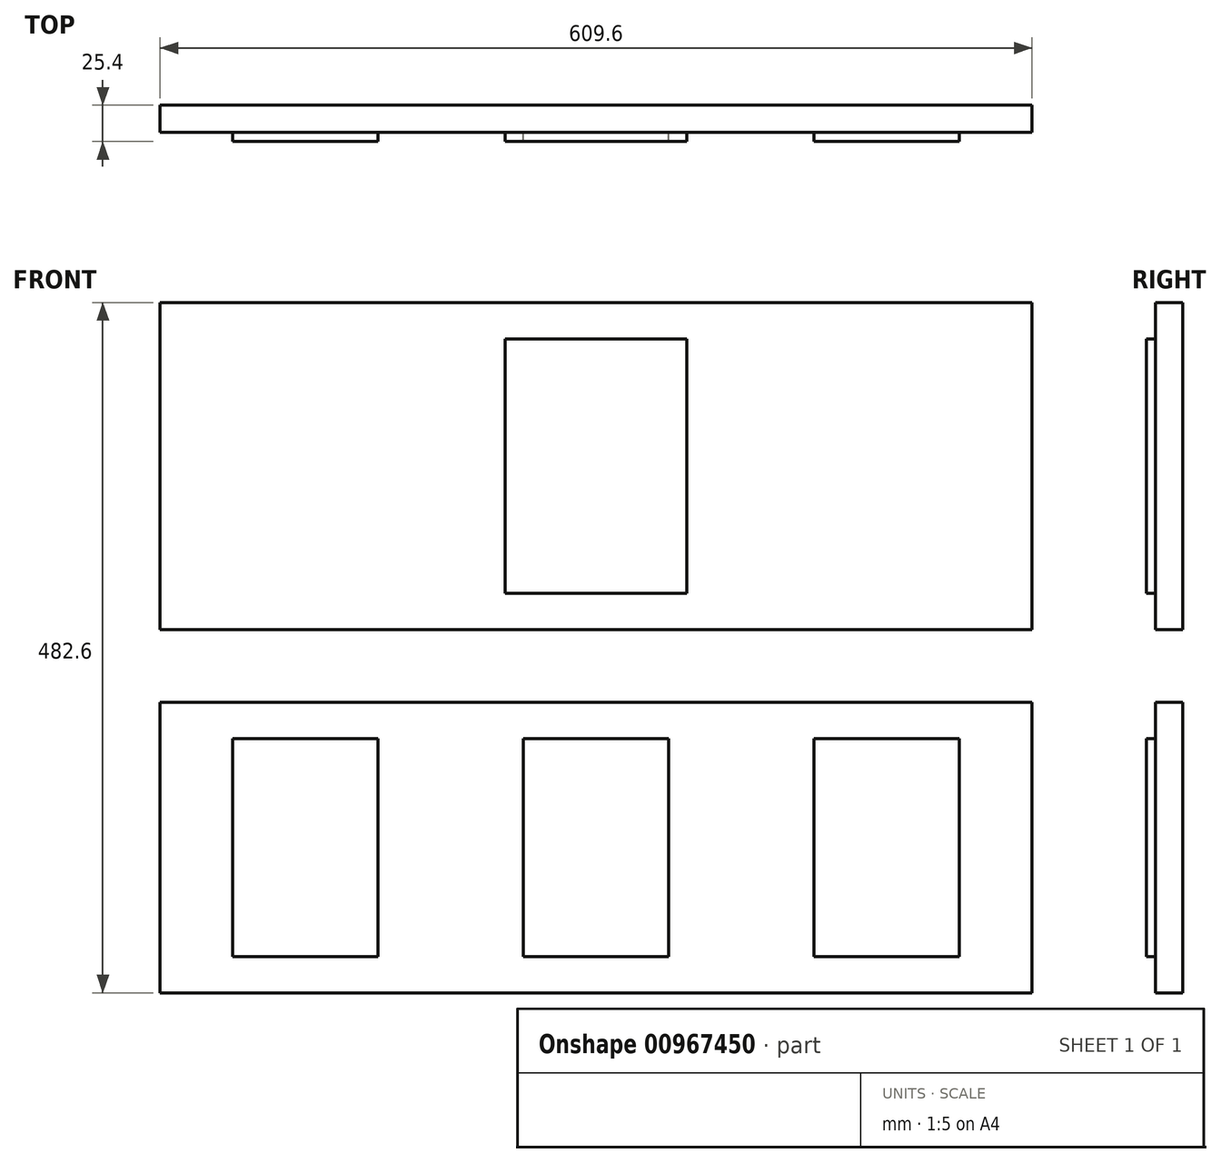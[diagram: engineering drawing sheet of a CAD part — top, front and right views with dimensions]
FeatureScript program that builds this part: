
annotation { "Feature Type Name" : "Feature", "Feature Type Description" : "" }
export const myFeature = defineFeature(function(context is Context, id is Id, definition is map)
    precondition{}
    {
        {
            var Q0;
            Q0=qCreatedBy(makeId("Front.planeOp"),FACE);
            var sketch = newSketch(context, id + "F0", { "sketchPlane" : qUnion([Q0])});
            skLineSegment(sketch, "E0.bottom", {"start": v(-63.5, 177.8) * mm, "end": v(63.5, 177.8) * mm});
            skLineSegment(sketch, "E0.top", {"start": v(-63.5, 0) * mm, "end": v(63.5, 0) * mm});
            skLineSegment(sketch, "E0.left", {"start": v(-63.5, 177.8) * mm, "end": v(-63.5, 0) * mm});
            skLineSegment(sketch, "E0.right", {"start": v(63.5, 177.8) * mm, "end": v(63.5, 0) * mm});
            skSolve(sketch);
        }
        {
            var Q0;
            Q0 = qSketchRegion(id + "F0", true);
            extrude(context, id + "F1", {"entities" : qUnion([Q0]), "depth" : 6.35 * mm, "offsetDistance" : 25.4 * mm});
        }
        {
            var Q0;
            Q0=qCreatedBy(makeId("Front.planeOp"),FACE);
            var sketch = newSketch(context, id + "F2", { "sketchPlane" : qUnion([Q0])});
            skLineSegment(sketch, "E1.bottom", {"start": v(-304.8, 203.2) * mm, "end": v(304.8, 203.2) * mm});
            skLineSegment(sketch, "E1.top", {"start": v(-304.8, -25.4) * mm, "end": v(304.8, -25.4) * mm});
            skLineSegment(sketch, "E1.left", {"start": v(-304.8, 203.2) * mm, "end": v(-304.8, -25.4) * mm});
            skLineSegment(sketch, "E1.right", {"start": v(304.8, 203.2) * mm, "end": v(304.8, -25.4) * mm});
            skLineSegment(sketch, "E2", {"start": v(0, 0) * mm, "end": v(0, -25.4) * mm, "construction": true});
            skLineSegment(sketch, "E3", {"start": v(-304.8, 88.9) * mm, "end": v(-63.5, 88.9) * mm, "construction": true});
            skSolve(sketch);
        }
        {
            var Q0;
            Q0 = qSketchRegion(id + "F2", true);
            extrude(context, id + "F3", {"entities" : qUnion([Q0]), "operationType" : NewBodyOperationType.ADD, "oppositeDirection" : true, "depth" : 19.05 * mm, "offsetDistance" : 25.4 * mm});
        }
        {
            var Q0;
            Q0=qCreatedBy(makeId("Front.planeOp"),FACE);
            var sketch = newSketch(context, id + "F4", { "sketchPlane" : qUnion([Q0])});
            skLineSegment(sketch, "E4.bottom", {"start": v(-50.8, -101.6) * mm, "end": v(50.8, -101.6) * mm});
            skLineSegment(sketch, "E4.top", {"start": v(-50.8, -254) * mm, "end": v(50.8, -254) * mm});
            skLineSegment(sketch, "E4.left", {"start": v(-50.8, -101.6) * mm, "end": v(-50.8, -254) * mm});
            skLineSegment(sketch, "E4.right", {"start": v(50.8, -101.6) * mm, "end": v(50.8, -254) * mm});
            skLineSegment(sketch, "E5.bottom", {"start": v(152.4, -101.6) * mm, "end": v(254, -101.6) * mm});
            skLineSegment(sketch, "E5.top", {"start": v(152.4, -254) * mm, "end": v(254, -254) * mm});
            skLineSegment(sketch, "E5.left", {"start": v(152.4, -101.6) * mm, "end": v(152.4, -254) * mm});
            skLineSegment(sketch, "E5.right", {"start": v(254, -101.6) * mm, "end": v(254, -254) * mm});
            skLineSegment(sketch, "E6.bottom", {"start": v(-152.4, -101.6) * mm, "end": v(-254, -101.6) * mm});
            skLineSegment(sketch, "E6.top", {"start": v(-152.4, -254) * mm, "end": v(-254, -254) * mm});
            skLineSegment(sketch, "E6.left", {"start": v(-152.4, -101.6) * mm, "end": v(-152.4, -254) * mm});
            skLineSegment(sketch, "E6.right", {"start": v(-254, -101.6) * mm, "end": v(-254, -254) * mm});
            skLineSegment(sketch, "E7", {"start": v(-152.4, -254) * mm, "end": v(-50.8, -254) * mm, "construction": true});
            skLineSegment(sketch, "E8", {"start": v(50.8, -254) * mm, "end": v(152.4, -254) * mm, "construction": true});
            skLineSegment(sketch, "E9", {"start": v(0, -101.6) * mm, "end": v(0, 0) * mm, "construction": true});
            skSolve(sketch);
        }
        {
            var Q0;
            Q0 = qSketchRegion(id + "F4", true);
            extrude(context, id + "F5", {"entities" : qUnion([Q0]), "depth" : 6.35 * mm, "offsetDistance" : 25.4 * mm});
        }
        {
            var Q0;
            Q0=qCreatedBy(makeId("Front.planeOp"),FACE);
            var sketch = newSketch(context, id + "F6", { "sketchPlane" : qUnion([Q0])});
            skLineSegment(sketch, "E10.bottom", {"start": v(-304.8, -76.2) * mm, "end": v(304.8, -76.2) * mm});
            skLineSegment(sketch, "E10.top", {"start": v(-304.8, -279.4) * mm, "end": v(304.8, -279.4) * mm});
            skLineSegment(sketch, "E10.left", {"start": v(-304.8, -76.2) * mm, "end": v(-304.8, -279.4) * mm});
            skLineSegment(sketch, "E10.right", {"start": v(304.8, -76.2) * mm, "end": v(304.8, -279.4) * mm});
            skLineSegment(sketch, "E11", {"start": v(0, 0) * mm, "end": v(0, -76.2) * mm});
            skLineSegment(sketch, "E12", {"start": v(-304.8, -177.8) * mm, "end": v(-50.8, -177.8) * mm});
            skSolve(sketch);
        }
        {
            var Q0;
            Q0 = qSketchRegion(id + "F6", true);
            extrude(context, id + "F7", {"entities" : qUnion([Q0]), "oppositeDirection" : true, "depth" : 19.05 * mm, "offsetDistance" : 25.4 * mm});
        }
    });
